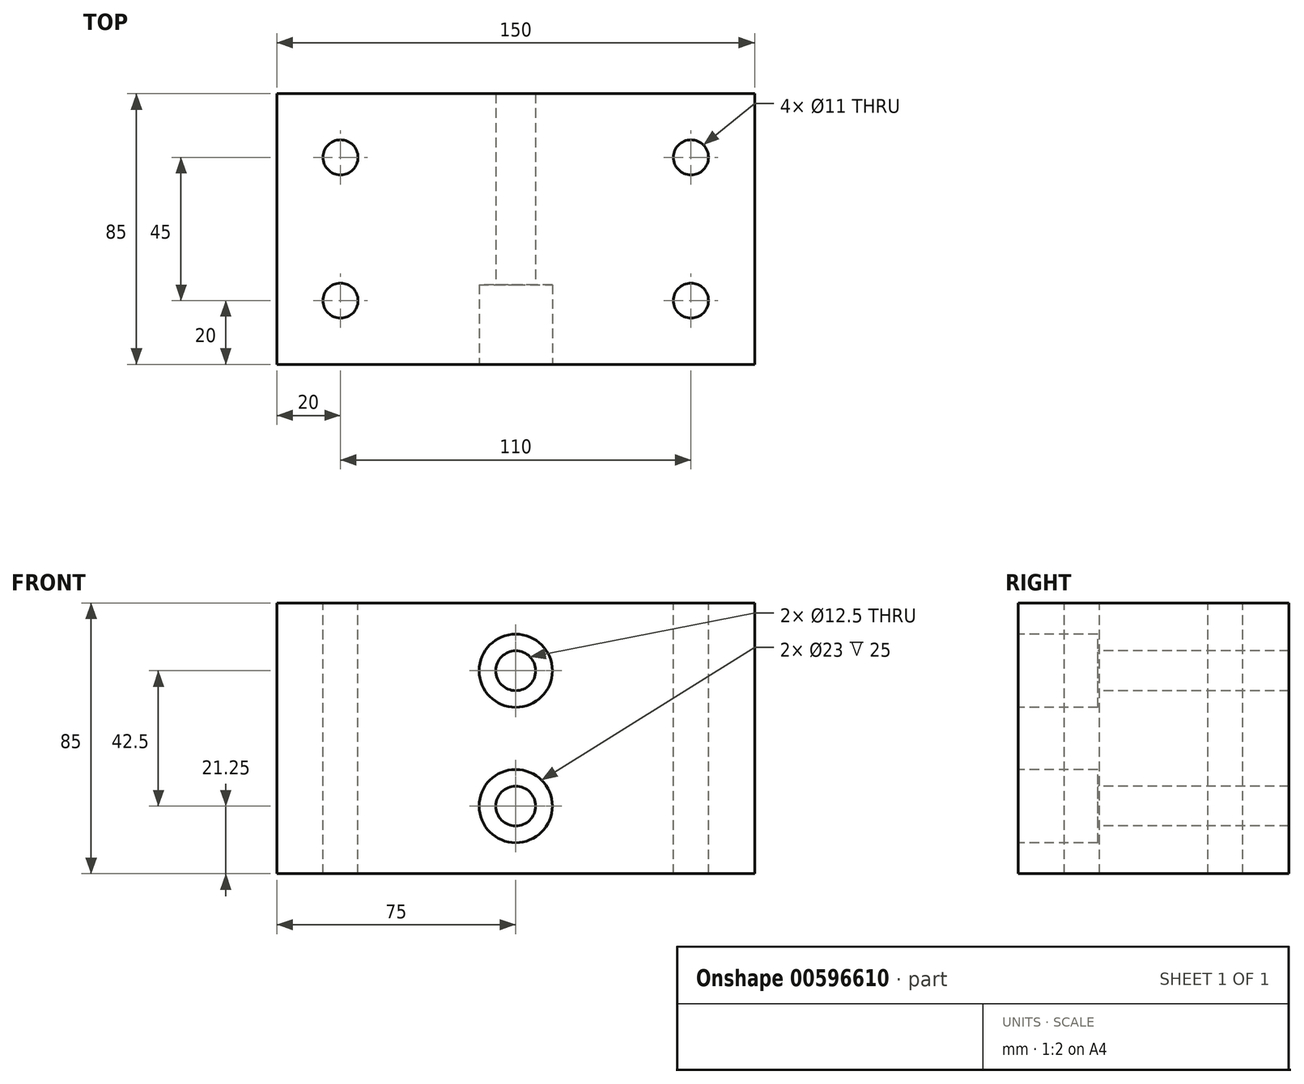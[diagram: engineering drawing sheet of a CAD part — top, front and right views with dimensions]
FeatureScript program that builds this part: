
annotation { "Feature Type Name" : "Feature", "Feature Type Description" : "" }
export const myFeature = defineFeature(function(context is Context, id is Id, definition is map)
    precondition{}
    {
        {
            var Q0;
            Q0=qCreatedBy(makeId("Top.planeOp"),FACE);
            var sketch = newSketch(context, id + "F0", { "sketchPlane" : qUnion([Q0])});
            skLineSegment(sketch, "E0.bottom", {"start": v(0, 0) * mm, "end": v(150, 0) * mm});
            skLineSegment(sketch, "E0.top", {"start": v(0, 85) * mm, "end": v(150, 85) * mm});
            skLineSegment(sketch, "E0.left", {"start": v(0, 0) * mm, "end": v(0, 85) * mm});
            skLineSegment(sketch, "E0.right", {"start": v(150, 0) * mm, "end": v(150, 85) * mm});
            skSolve(sketch);
        }
        {
            var Q0;
            Q0 = qSketchRegion(id + "F0", true);
            extrude(context, id + "F1", {"entities" : qUnion([Q0]), "depth" : 85 * mm, "offsetDistance" : 25 * mm});
        }
        {
            var Q0;
            Q0=makeQuery(id+"F1.opExtrude","SWEPT_FACE",FACE,{"disambiguationData":[OSD([sQuery(id+"F0.wireOp",EDGE,"E0.bottom")])]});
            var sketch = newSketch(context, id + "F2", { "sketchPlane" : qUnion([Q0])});
            skCircle(sketch, "E1", {"center": v(75, 63.75) * mm, "radius": 11.5 * mm});
            skCircle(sketch, "E2", {"center": v(75, 63.75) * mm, "radius": 6.25 * mm});
            skCircle(sketch, "E3.0.1.0", {"center": v(75, 21.25) * mm, "radius": 6.25 * mm});
            skCircle(sketch, "E3.0.1.1", {"center": v(75, 21.25) * mm, "radius": 11.5 * mm});
            skLineSegment(sketch, "E3.direction1", {"start": v(75, 63.75) * mm, "end": v(100, 63.75) * mm, "construction": true});
            skLineSegment(sketch, "E3.direction2", {"start": v(75, 63.75) * mm, "end": v(75, 21.25) * mm, "construction": true});
            skSolve(sketch);
        }
        {
            var Q0;
            Q0=makeQuery(id+"F2.imprint","IMPRINT",FACE,{"disambiguationData":[TD([[makeQuery(id+"F2.imprint","IMPRINT",EDGE,{"derivedFrom":sQuery(id+"F2.wireOp",EDGE,"E2")}),1.0]])]});
            var Q1;
            Q1=makeQuery(id+"F2.imprint","IMPRINT",FACE,{"disambiguationData":[TD([[makeQuery(id+"F2.imprint","IMPRINT",EDGE,{"derivedFrom":sQuery(id+"F2.wireOp",EDGE,"E3.0.1.0")}),1.0]])]});
            extrude(context, id + "F3", {"entities" : qUnion([Q0, Q1]), "operationType" : NewBodyOperationType.REMOVE, "endBound" : BoundingType.THROUGH_ALL, "oppositeDirection" : true, "depth" : 25 * mm, "offsetDistance" : 25 * mm});
        }
        {
            var Q0;
            Q0=makeQuery(id+"F2.imprint","IMPRINT",FACE,{"disambiguationData":[TD([[makeQuery(id+"F2.imprint","IMPRINT",EDGE,{"derivedFrom":sQuery(id+"F2.wireOp",EDGE,"E1")}),1.0]])]});
            var Q1;
            Q1=makeQuery(id+"F2.imprint","IMPRINT",FACE,{"disambiguationData":[TD([[makeQuery(id+"F2.imprint","IMPRINT",EDGE,{"derivedFrom":sQuery(id+"F2.wireOp",EDGE,"E3.0.1.0")}),-1.0]])]});
            extrude(context, id + "F4", {"entities" : qUnion([Q0, Q1]), "operationType" : NewBodyOperationType.REMOVE, "oppositeDirection" : true, "depth" : 25 * mm, "offsetDistance" : 25 * mm});
        }
        {
            var Q0;
            Q0=makeQuery(id+"F1.opExtrude","CAP_FACE",FACE,{"disambiguationData":[OSD([sQuery(id+"F0.wireOp",EDGE,"E0.bottom"),sQuery(id+"F0.wireOp",EDGE,"E0.top"),sQuery(id+"F0.wireOp",EDGE,"E0.left"),sQuery(id+"F0.wireOp",EDGE,"E0.right")])],"isStart":false});
            var sketch = newSketch(context, id + "F5", { "sketchPlane" : qUnion([Q0])});
            skPoint(sketch, "E4", {"position": v(20, 65) * mm});
            skPoint(sketch, "E5", {"position": v(130, 65) * mm});
            skPoint(sketch, "E6", {"position": v(130, 20) * mm});
            skPoint(sketch, "E7", {"position": v(20, 20) * mm});
            skPoint(sketch, "E8", {"position": v(-137.09, 28.62) * mm});
            skSolve(sketch);
        }
        {
            var Q0;
            Q0=sQuery(id+"F5.wireOp",VERTEX,"E4");
            var Q1;
            Q1=sQuery(id+"F5.wireOp",VERTEX,"E7");
            var Q2;
            Q2=sQuery(id+"F5.wireOp",VERTEX,"E6");
            var Q3;
            Q3=sQuery(id+"F5.wireOp",VERTEX,"E5");
            var Q4;
            Q4=makeQuery(id+"F1.opExtrude","SWEPT_BODY",BODY,{"disambiguationData":[OSD([sQuery(id+"F0.wireOp",EDGE,"E0.bottom"),sQuery(id+"F0.wireOp",EDGE,"E0.top"),sQuery(id+"F0.wireOp",EDGE,"E0.left"),sQuery(id+"F0.wireOp",EDGE,"E0.right")])]});
            hole(context, id + "F6", {"style" : HoleStyle.SIMPLE, "endStyle" : HoleEndStyle.THROUGH, "standardTappedOrClearance" : lookupTablePath({ "standard" : "ISO", "fit" : "Normal", "size" : "M10", "type" : "Clearance" }), "standardBlindInLast" : lookupTablePath({ "fit" : "Standard", "standard" : "ISO", "size" : "M10", "type" : "Clearance" }), "holeDiameter" : 11 * mm, "majorDiameter" : 5 * mm, "isTappedThrough" : true, "tappedDepth" : 12 * mm, "tapClearance" : 3, "startFromSketch" : true, "locations" : qUnion([Q0, Q1, Q2, Q3]), "scope" : qUnion([Q4])});
        }
    });
